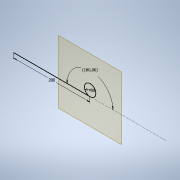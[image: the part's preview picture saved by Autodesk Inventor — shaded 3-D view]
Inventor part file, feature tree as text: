
AUTODESK INVENTOR PART (.ipt)
format: ipt  version: 2021 (Build 250183000, 183)  size: 138,240 bytes
history: native  units: mm
features: other x3, sketch x2, sweep x1
ambient origin geometry x8: Origin, YZ Plane, XZ Plane, XY Plane, X Axis, Y Axis, Z Axis, Center Point
bodies: Body1 (feature_tree)
feature tree (6):
  other  "Bryła1"
  other  "Płaszczyzna konstrukcyjna1"
  sketch  "Szkic1"
  other  "Płaszczyzna konstrukcyjna2"
  sweep  "Przeciągnięcie1"
  sketch  "Szkic2"
